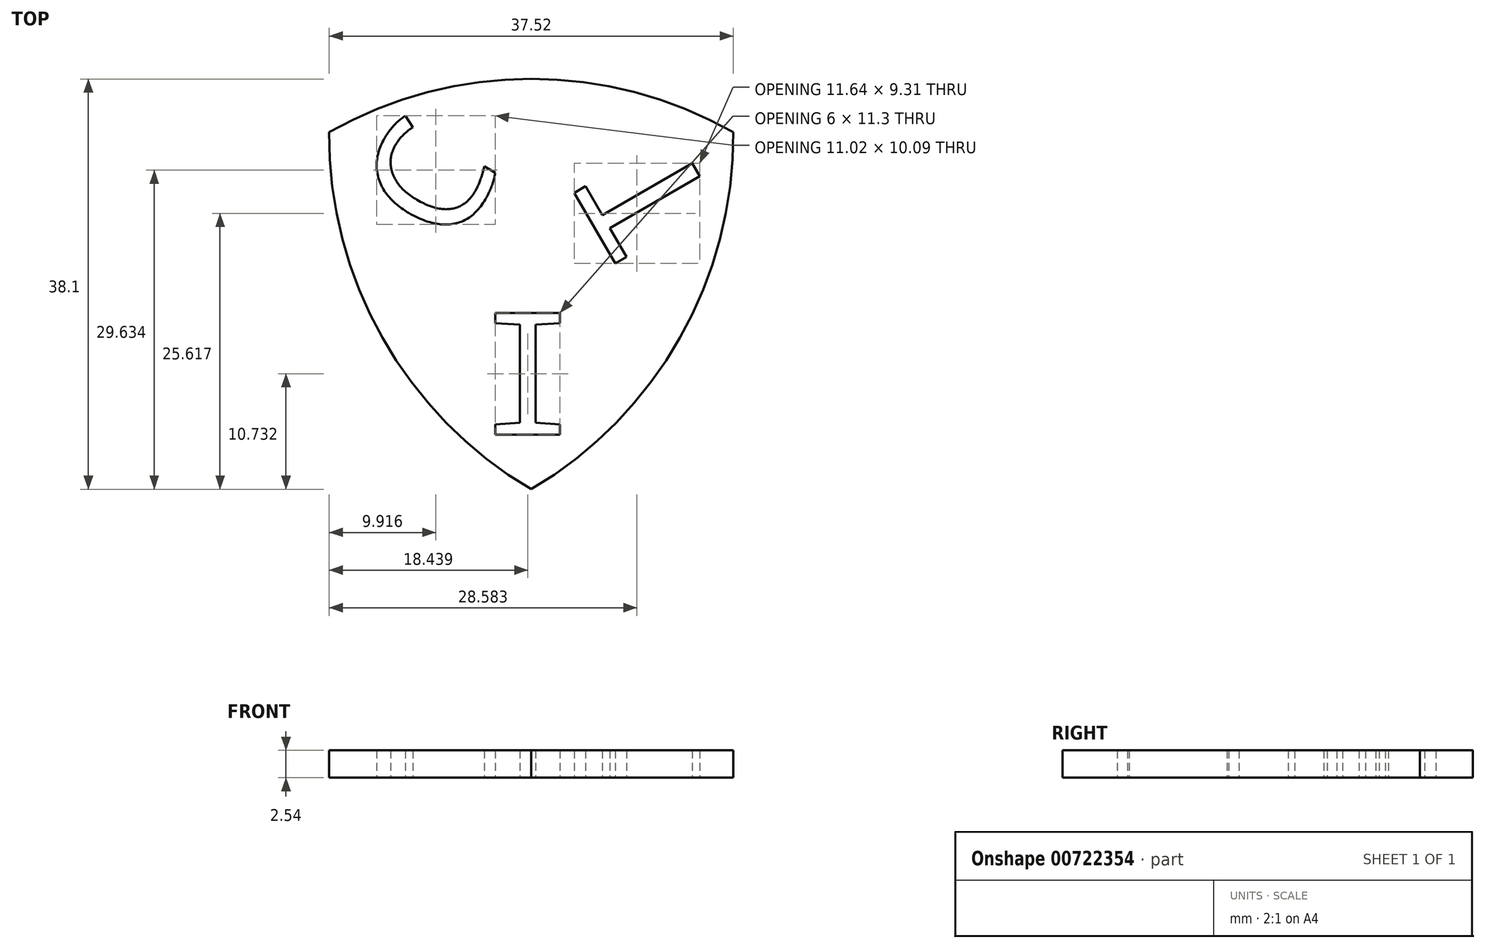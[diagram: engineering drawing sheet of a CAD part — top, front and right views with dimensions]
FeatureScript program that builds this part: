
annotation { "Feature Type Name" : "Feature", "Feature Type Description" : "" }
export const myFeature = defineFeature(function(context is Context, id is Id, definition is map)
    precondition{}
    {
        {
            var Q0;
            Q0=qCreatedBy(makeId("Top.planeOp"),FACE);
            var sketch = newSketch(context, id + "F0", { "sketchPlane" : qUnion([Q0])});
            skCircle(sketch, "E0", {"center": v(0, 0) * mm, "radius": 38.1 * mm});
            skSolve(sketch);
        }
        {
            var Q0;
            Q0=qCreatedBy(makeId("Top.planeOp"),FACE);
            var sketch = newSketch(context, id + "F1", { "sketchPlane" : qUnion([Q0])});
            skCircle(sketch, "E1", {"center": v(-38.68, 0) * mm, "radius": 38.1 * mm});
            skSolve(sketch);
        }
        {
            var Q0;
            Q0=qCreatedBy(makeId("Top.planeOp"),FACE);
            var sketch = newSketch(context, id + "F2", { "sketchPlane" : qUnion([Q0])});
            skCircle(sketch, "E2", {"center": v(-19.34, -32.83) * mm, "radius": 38.1 * mm});
            skSolve(sketch);
        }
        {
            var Q0;
            Q0=makeQuery(id+"F0.imprint","IMPRINT",FACE,{"disambiguationData":[TD([[makeQuery(id+"F0.imprint","IMPRINT",EDGE,{"derivedFrom":sQuery(id+"F0.wireOp",EDGE,"E0")}),1.0]])]});
            extrude(context, id + "F3", {"entities" : qUnion([Q0]), "depth" : 2.54 * mm, "offsetDistance" : 25.4 * mm});
        }
        {
            var Q0;
            Q0=makeQuery(id+"F1.imprint","IMPRINT",FACE,{"disambiguationData":[TD([[makeQuery(id+"F1.imprint","IMPRINT",EDGE,{"derivedFrom":sQuery(id+"F1.wireOp",EDGE,"E1")}),1.0]])]});
            extrude(context, id + "F4", {"entities" : qUnion([Q0]), "depth" : 2.54 * mm, "offsetDistance" : 25.4 * mm});
        }
        {
            var Q0;
            Q0=makeQuery(id+"F2.imprint","IMPRINT",FACE,{"disambiguationData":[TD([[makeQuery(id+"F2.imprint","IMPRINT",EDGE,{"derivedFrom":sQuery(id+"F2.wireOp",EDGE,"E2")}),1.0]])]});
            extrude(context, id + "F5", {"entities" : qUnion([Q0]), "depth" : 2.54 * mm, "offsetDistance" : 25.4 * mm});
        }
        {
            var Q0;
            Q0=makeQuery(id+"F4.opExtrude","SWEPT_BODY",BODY,{"disambiguationData":[OSD([sQuery(id+"F1.wireOp",EDGE,"E1")])]});
            var Q1;
            Q1=makeQuery(id+"F3.opExtrude","SWEPT_BODY",BODY,{"disambiguationData":[OSD([sQuery(id+"F0.wireOp",EDGE,"E0")])]});
            var Q2;
            Q2=makeQuery(id+"F5.opExtrude","SWEPT_BODY",BODY,{"disambiguationData":[OSD([sQuery(id+"F2.wireOp",EDGE,"E2")])]});
            booleanBodies(context, id + "F6", {"operationType" : BooleanOperationType.INTERSECTION, "tools" : qUnion([Q0, Q1, Q2])});
        }
        {
            var Q0;
            Q0=qCreatedBy(makeId("Top.planeOp"),FACE);
            var sketch = newSketch(context, id + "F7", { "sketchPlane" : qUnion([Q0])});
            skText(sketch, "E3", { "text": "C", "fontName": "DroidSansMono.ttf"});
            skText(sketch, "E4", { "text": "I", "fontName": "DroidSansMono.ttf"});
            skText(sketch, "E5", { "text": "T", "fontName": "DroidSansMono.ttf"});
            const initialGuessF7  = {"E3": [-0.02652, -0.01067, 0.5, 0.86603, 0.01073], "E4": [-0.0244, -0.02775, 1, 0, 0.0114], "E5": [-0.00177, -0.0071, -0.5, 0.86603, 0.01094]};
            skSetInitialGuess(sketch, initialGuessF7);
            skSolve(sketch);
        }
        {
            var Q0;
            Q0 = qSketchRegion(id + "F7", true);
            extrude(context, id + "F8", {"entities" : qUnion([Q0]), "depth" : 2.54 * mm, "offsetDistance" : 25.4 * mm});
        }
        {
            var Q0;
            Q0=makeQuery(id+"F8.opExtrude","SWEPT_BODY",BODY,{"disambiguationData":[OSD([sQuery(id+"F7.wireOp",EDGE,"E3.sketch_text.stroke-0"),sQuery(id+"F7.wireOp",EDGE,"E3.sketch_text.stroke-1"),sQuery(id+"F7.wireOp",EDGE,"E3.sketch_text.stroke-2"),sQuery(id+"F7.wireOp",EDGE,"E3.sketch_text.stroke-3"),sQuery(id+"F7.wireOp",EDGE,"E3.sketch_text.stroke-4"),sQuery(id+"F7.wireOp",EDGE,"E3.sketch_text.stroke-5"),sQuery(id+"F7.wireOp",EDGE,"E3.sketch_text.stroke-6"),sQuery(id+"F7.wireOp",EDGE,"E3.sketch_text.stroke-7"),sQuery(id+"F7.wireOp",EDGE,"E3.sketch_text.stroke-8"),sQuery(id+"F7.wireOp",EDGE,"E3.sketch_text.stroke-9"),sQuery(id+"F7.wireOp",EDGE,"E3.sketch_text.stroke-10"),sQuery(id+"F7.wireOp",EDGE,"E3.sketch_text.stroke-11"),sQuery(id+"F7.wireOp",EDGE,"E3.sketch_text.stroke-12"),sQuery(id+"F7.wireOp",EDGE,"E3.sketch_text.stroke-13")])]});
            var Q1;
            Q1=makeQuery(id+"F8.opExtrude","SWEPT_BODY",BODY,{"disambiguationData":[OSD([sQuery(id+"F7.wireOp",EDGE,"E4.sketch_text.stroke-0"),sQuery(id+"F7.wireOp",EDGE,"E4.sketch_text.stroke-1"),sQuery(id+"F7.wireOp",EDGE,"E4.sketch_text.stroke-2"),sQuery(id+"F7.wireOp",EDGE,"E4.sketch_text.stroke-3"),sQuery(id+"F7.wireOp",EDGE,"E4.sketch_text.stroke-4"),sQuery(id+"F7.wireOp",EDGE,"E4.sketch_text.stroke-5"),sQuery(id+"F7.wireOp",EDGE,"E4.sketch_text.stroke-6"),sQuery(id+"F7.wireOp",EDGE,"E4.sketch_text.stroke-7"),sQuery(id+"F7.wireOp",EDGE,"E4.sketch_text.stroke-8"),sQuery(id+"F7.wireOp",EDGE,"E4.sketch_text.stroke-9"),sQuery(id+"F7.wireOp",EDGE,"E4.sketch_text.stroke-10"),sQuery(id+"F7.wireOp",EDGE,"E4.sketch_text.stroke-11")])]});
            var Q2;
            Q2=makeQuery(id+"F8.opExtrude","SWEPT_BODY",BODY,{"disambiguationData":[OSD([sQuery(id+"F7.wireOp",EDGE,"E5.sketch_text.stroke-0"),sQuery(id+"F7.wireOp",EDGE,"E5.sketch_text.stroke-1"),sQuery(id+"F7.wireOp",EDGE,"E5.sketch_text.stroke-2"),sQuery(id+"F7.wireOp",EDGE,"E5.sketch_text.stroke-3"),sQuery(id+"F7.wireOp",EDGE,"E5.sketch_text.stroke-4"),sQuery(id+"F7.wireOp",EDGE,"E5.sketch_text.stroke-5"),sQuery(id+"F7.wireOp",EDGE,"E5.sketch_text.stroke-6"),sQuery(id+"F7.wireOp",EDGE,"E5.sketch_text.stroke-7")])]});
            var Q3;
            Q3=makeQuery(id+"F6.opBoolean","INTERSECT",BODY,{"derivedFrom":[makeQuery(id+"F3.opExtrude","SWEPT_BODY",BODY,{"disambiguationData":[OSD([sQuery(id+"F0.wireOp",EDGE,"E0")])]}),makeQuery(id+"F4.opExtrude","SWEPT_BODY",BODY,{"disambiguationData":[OSD([sQuery(id+"F1.wireOp",EDGE,"E1")])]}),makeQuery(id+"F5.opExtrude","SWEPT_BODY",BODY,{"disambiguationData":[OSD([sQuery(id+"F2.wireOp",EDGE,"E2")])]})]});
            booleanBodies(context, id + "F9", {"operationType" : BooleanOperationType.SUBTRACTION, "tools" : qUnion([Q0, Q1, Q2]), "targets" : qUnion([Q3])});
        }
    });
